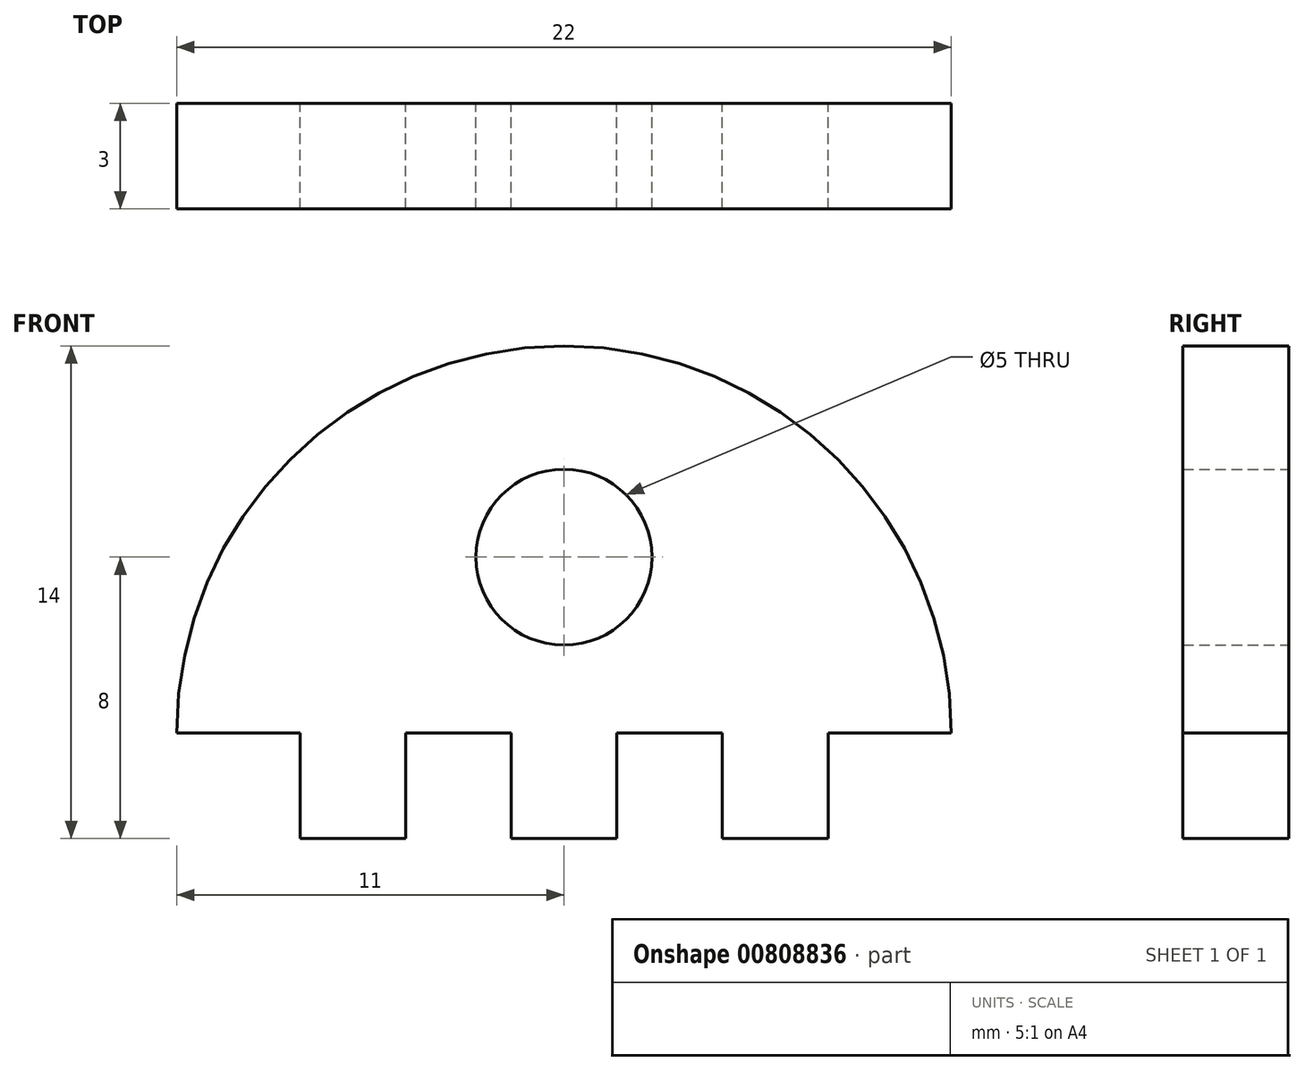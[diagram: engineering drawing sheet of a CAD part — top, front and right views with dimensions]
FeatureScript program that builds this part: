
annotation { "Feature Type Name" : "Feature", "Feature Type Description" : "" }
export const myFeature = defineFeature(function(context is Context, id is Id, definition is map)
    precondition{}
    {
        {
            var Q0;
            Q0=qCreatedBy(makeId("Front.planeOp"),FACE);
            var sketch = newSketch(context, id + "F0", { "sketchPlane" : qUnion([Q0])});
            skCircle(sketch, "E0", {"center": v(0, 0) * mm, "radius": 11 * mm});
            skLineSegment(sketch, "E1", {"start": v(-11, 0) * mm, "end": v(-6, 0) * mm});
            skLineSegment(sketch, "E2.bottom", {"start": v(-1.5, -3) * mm, "end": v(1.5, -3) * mm});
            skLineSegment(sketch, "E2.left", {"start": v(-1.5, -3) * mm, "end": v(-1.5, 0) * mm});
            skLineSegment(sketch, "E2.right", {"start": v(1.5, -3) * mm, "end": v(1.5, 0) * mm});
            skLineSegment(sketch, "E3.bottom", {"start": v(-4.5, -3) * mm, "end": v(-7.5, -3) * mm});
            skLineSegment(sketch, "E3.top", {"start": v(-4.5, 3) * mm, "end": v(-7.5, 3) * mm});
            skLineSegment(sketch, "E3.left", {"start": v(-4.5, -3) * mm, "end": v(-4.5, 0) * mm});
            skLineSegment(sketch, "E3.right", {"start": v(-7.5, -3) * mm, "end": v(-7.5, 3) * mm});
            skPoint(sketch, "E3.middle", {"position": v(-6, 0) * mm});
            skLineSegment(sketch, "E4.bottom", {"start": v(4.5, -3) * mm, "end": v(7.5, -3) * mm});
            skLineSegment(sketch, "E4.top", {"start": v(4.5, 3) * mm, "end": v(7.5, 3) * mm});
            skLineSegment(sketch, "E4.left", {"start": v(4.5, -3) * mm, "end": v(4.5, 0) * mm});
            skLineSegment(sketch, "E4.right", {"start": v(7.5, -3) * mm, "end": v(7.5, 3) * mm});
            skPoint(sketch, "E4.middle", {"position": v(6, 0) * mm});
            skCircle(sketch, "E5", {"center": v(0, 5) * mm, "radius": 2.5 * mm});
            skPoint(sketch, "E6.orphan", {"position": v(-1.5, 3) * mm});
            skPoint(sketch, "E7.orphan", {"position": v(1.5, 3) * mm});
            skLineSegment(sketch, "E8.trimOffspring", {"start": v(1.5, 0) * mm, "end": v(4.5, 0) * mm});
            skLineSegment(sketch, "E9.trimOffspring", {"start": v(-4.5, 0) * mm, "end": v(-1.5, 0) * mm});
            skLineSegment(sketch, "E10.trimOffspring", {"start": v(6, 0) * mm, "end": v(11, 0) * mm});
            skSolve(sketch);
        }
        {
            var Q0;
            {var subQ5=sQuery(id+"F0.wireOp",EDGE,"E2.top");Q0=makeQuery(id+"F0.imprint","IMPRINT",FACE,{"disambiguationData":[TD([[makeQuery(id+"F0.imprint","IMPRINT",EDGE,{"derivedFrom":subQ5}),1.0]])]});}
            var Q1;
            {var subQ5=sQuery(id+"F0.wireOp",EDGE,"E3.bottom");Q1=makeQuery(id+"F0.imprint","IMPRINT",FACE,{"disambiguationData":[TD([[makeQuery(id+"F0.imprint","IMPRINT",EDGE,{"derivedFrom":subQ5}),-1.0]])]});}
            var Q2;
            {var subQ5=sQuery(id+"F0.wireOp",EDGE,"E2.bottom");Q2=makeQuery(id+"F0.imprint","IMPRINT",FACE,{"disambiguationData":[TD([[makeQuery(id+"F0.imprint","IMPRINT",EDGE,{"derivedFrom":subQ5}),1.0]])]});}
            var Q3;
            {var subQ5=sQuery(id+"F0.wireOp",EDGE,"E4.bottom");Q3=makeQuery(id+"F0.imprint","IMPRINT",FACE,{"disambiguationData":[TD([[makeQuery(id+"F0.imprint","IMPRINT",EDGE,{"derivedFrom":subQ5}),1.0]])]});}
            var Q4;
            {var subQ5=sQuery(id+"F0.wireOp",EDGE,"E4.top");Q4=makeQuery(id+"F0.imprint","IMPRINT",FACE,{"disambiguationData":[TD([[makeQuery(id+"F0.imprint","IMPRINT",EDGE,{"derivedFrom":subQ5}),-1.0]])]});}
            var Q5;
            {var subQ5=sQuery(id+"F0.wireOp",EDGE,"E2.top");Q5=makeQuery(id+"F0.imprint","IMPRINT",FACE,{"disambiguationData":[TD([[makeQuery(id+"F0.imprint","IMPRINT",EDGE,{"derivedFrom":subQ5}),-1.0]])]});}
            var Q6;
            {var subQ5=sQuery(id+"F0.wireOp",EDGE,"E3.top");Q6=makeQuery(id+"F0.imprint","IMPRINT",FACE,{"disambiguationData":[TD([[makeQuery(id+"F0.imprint","IMPRINT",EDGE,{"derivedFrom":subQ5}),1.0]])]});}
            extrude(context, id + "F1", {"entities" : qUnion([Q0, Q1, Q2, Q3, Q4, Q5, Q6]), "depth" : 3 * mm, "offsetDistance" : 25 * mm});
        }
    });
